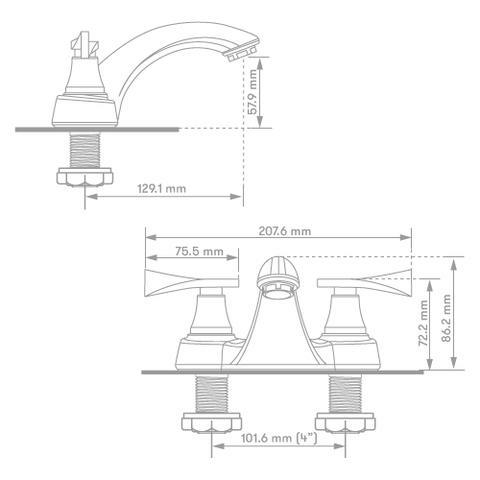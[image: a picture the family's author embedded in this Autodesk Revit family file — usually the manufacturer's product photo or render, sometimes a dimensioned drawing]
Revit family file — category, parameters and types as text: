
# Revit family: 01-0902-11 MEZCLADOR LAVAMANOS 4” HELVETIA
name_source: partatom
category: Plumbing Fixtures
revit_build: Autodesk Revit 2018 (Build: 20170223_1515(x64)
units: mm (PartAtom-declared; Revit-internal decimal feet)

## family parameters
Cut with Voids When Loaded = No
Host = Face
OmniClass Number = 23.31.11.00
Part Type = Normal
Room Calculation Point = No
Round Connector Dimension = Use Diameter
Shared = No

## types (1)
- 01-0902-11
    Alto Aireador = 57.9 mm  [stored 0.189961 ft]
    Ancho = 171.64 mm
    CW Connection = Yes
    Default Elevation = 0 mm  [stored 0 ft]
    Description = Bimando baño
    Eje (Rosca) = 101.64 mm  [stored 0.333465 ft]
    Eje-Aireador = 129.1 mm  [stored 0.423556 ft]
    HW Connection = Yes
    Link Ficha Tecnica = http://infotecnica.gricol.com
    Manija = 70 mm  [stored 0.229659 ft]
    Manufacturer = Gricol
    Model = 01-0902-11
    Plastico - ABS Cromado = Plastico - ABS Cromado
    Product Name = MEZCLADOR LAVAMANOS 4” HELVETIA
    Type Image = MEZCLADOR LAVAMANOS 4” HELVETIA.jpg
    URL = https://www.gricol.com
    Vent Connection = No
    Waste Connection = No

note: [stored X ft] marks values corroborated as IEEE doubles in the binary element streams (Revit-internal decimal feet)

## geometry (parser evidence)
native form markers: Blend x2, Sweep x2
no freeform markers — native parametric forms only
